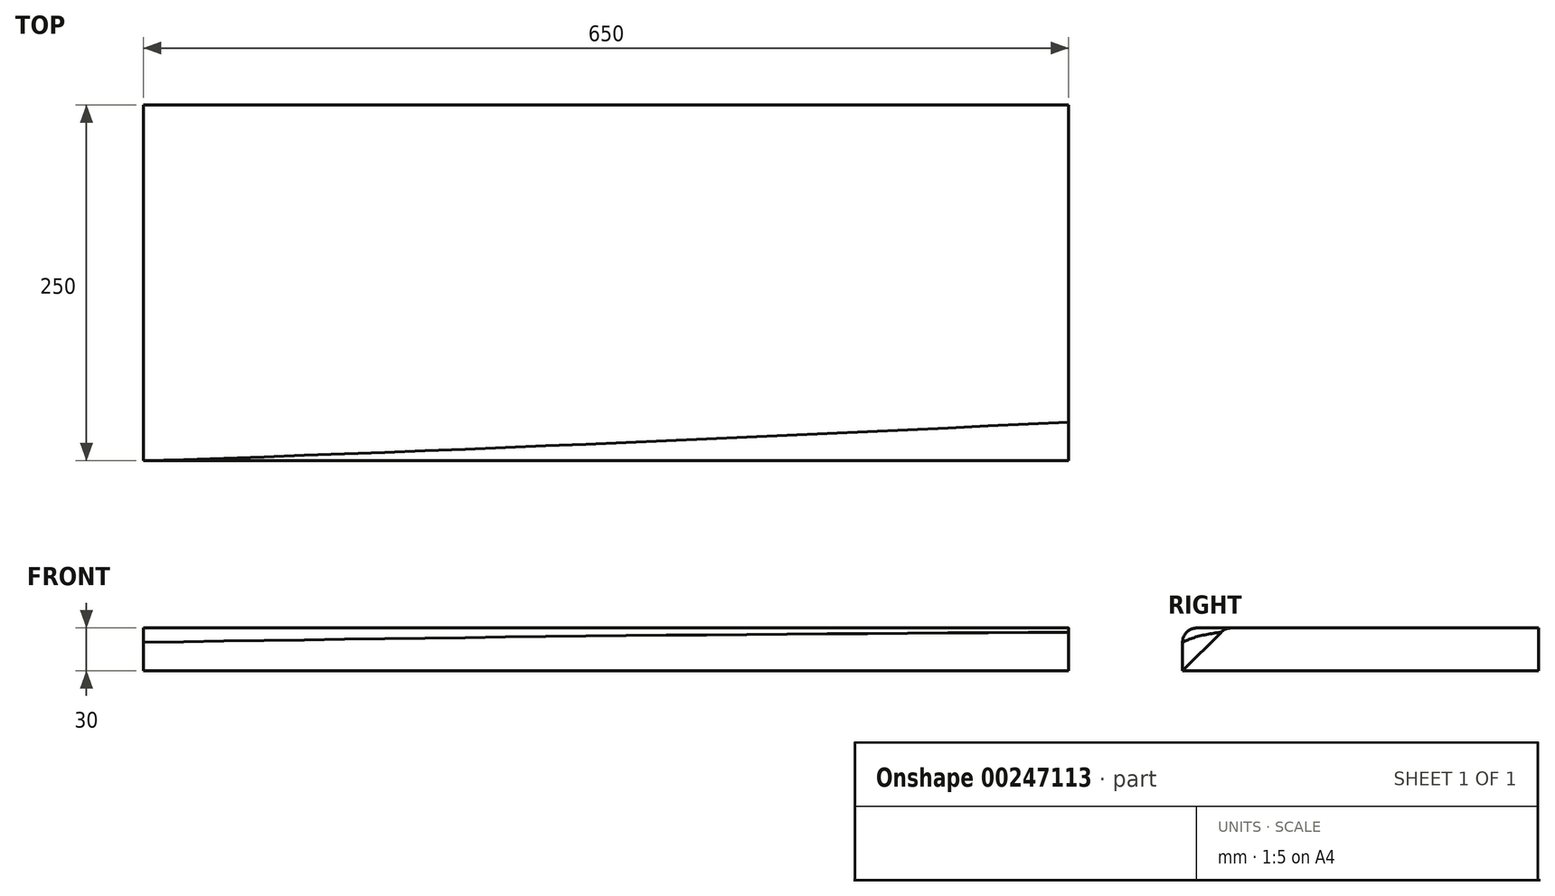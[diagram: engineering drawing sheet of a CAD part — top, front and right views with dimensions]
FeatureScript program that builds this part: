
annotation { "Feature Type Name" : "Feature", "Feature Type Description" : "" }
export const myFeature = defineFeature(function(context is Context, id is Id, definition is map)
    precondition{}
    {
        {
            var Q0;
            Q0=qCreatedBy(makeId("Right.planeOp"),FACE);
            var sketch = newSketch(context, id + "F0", { "sketchPlane" : qUnion([Q0])});
            skLineSegment(sketch, "E0.bottom", {"start": v(125, -15) * mm, "end": v(-125, -15) * mm});
            skLineSegment(sketch, "E0.top", {"start": v(125, 15) * mm, "end": v(-95, 15) * mm});
            skLineSegment(sketch, "E0.left", {"start": v(125, -15) * mm, "end": v(125, 15) * mm});
            skPoint(sketch, "E0.middle", {"position": v(0, 0) * mm});
            skLineSegment(sketch, "E1", {"start": v(-125, -15) * mm, "end": v(-95, 15) * mm});
            skPoint(sketch, "E2.orphan", {"position": v(-125, 15) * mm});
            skSolve(sketch);
        }
        {
            var Q0;
            Q0=qCreatedBy(makeId("Right.planeOp"),FACE);
            cPlane(context, id + "F1", {"entities" : qUnion([Q0]), "cplaneType" : CPlaneType.OFFSET, "offset" : 650 * mm, "oppositeDirection" : true, "width" : 150 * mm, "height" : 150 * mm});
        }
        {
            var Q0;
            Q0=qCreatedBy(id+"F1.planeOp",FACE);
            var sketch = newSketch(context, id + "F2", { "sketchPlane" : qUnion([Q0])});
            skLineSegment(sketch, "E3.0", {"start": v(125, -15) * mm, "end": v(-125, -15) * mm});
            skLineSegment(sketch, "E3.1", {"start": v(125, 15) * mm, "end": v(-125, 15) * mm});
            skLineSegment(sketch, "E3.2", {"start": v(125, -15) * mm, "end": v(125, 15) * mm});
            skPoint(sketch, "E3.3", {"position": v(0, 0) * mm});
            skLineSegment(sketch, "E4", {"start": v(-125, -15) * mm, "end": v(-125, 15) * mm});
            skSolve(sketch);
        }
        {
            var Q0;
            Q0=makeQuery(id+"F0.imprint","IMPRINT",FACE,{"disambiguationData":[TD([[makeQuery(id+"F0.imprint","IMPRINT",EDGE,{"derivedFrom":sQuery(id+"F0.wireOp",EDGE,"E0.bottom")}),-1.0]])]});
            var Q1;
            Q1=makeQuery(id+"F2.imprint","IMPRINT",FACE,{"disambiguationData":[TD([[makeQuery(id+"F2.imprint","IMPRINT",EDGE,{"derivedFrom":sQuery(id+"F2.wireOp",EDGE,"E3.0")}),-1.0]])]});
            loft(context, id + "F3", {"sheetProfilesArray" : [{ "sheetProfileEntities" : qUnion([Q0]) }, { "sheetProfileEntities" : qUnion([Q1]) }]});
        }
        {
            var Q0;
            Q0=makeQuery(id+"F3.opLoft","SWEPT_EDGE",EDGE,{"disambiguationData":[OSD([sQuery(id+"F0.wireOp",EDGE,"E0.top"),sQuery(id+"F0.wireOp",EDGE,"E1"),sQuery(id+"F2.wireOp",EDGE,"E3.1"),sQuery(id+"F2.wireOp",EDGE,"E4")])]});
            fillet(context, id + "F4", {"entities" : qUnion([Q0]), "radius" : 10 * mm, "tangentPropagation" : true, "allowEdgeOverflow" : false});
        }
    });
